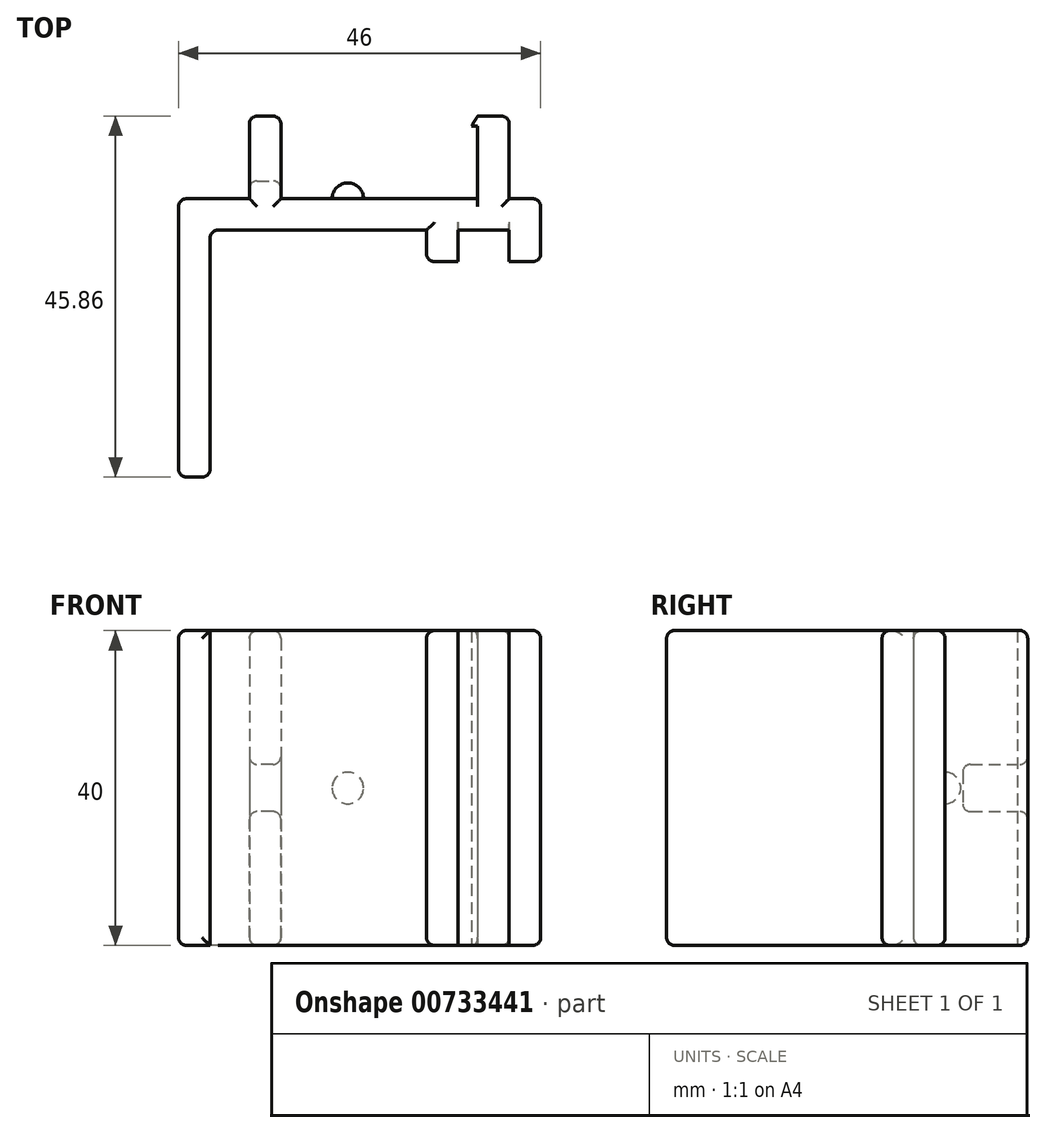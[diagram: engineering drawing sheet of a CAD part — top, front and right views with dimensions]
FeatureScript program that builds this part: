
annotation { "Feature Type Name" : "Feature", "Feature Type Description" : "" }
export const myFeature = defineFeature(function(context is Context, id is Id, definition is map)
    precondition{}
    {
        {
            var Q0;
            Q0=qCreatedBy(makeId("Top.planeOp"),FACE);
            var sketch = newSketch(context, id + "F0", { "sketchPlane" : qUnion([Q0])});
            skLineSegment(sketch, "E0", {"start": v(-21.66, 16.4) * mm, "end": v(-12.66, 16.4) * mm});
            skLineSegment(sketch, "E1", {"start": v(24.34, 16.4) * mm, "end": v(24.34, 8.4) * mm});
            skLineSegment(sketch, "E2", {"start": v(24.34, 8.4) * mm, "end": v(20.34, 8.4) * mm});
            skLineSegment(sketch, "E3", {"start": v(20.34, 8.4) * mm, "end": v(20.34, 12.4) * mm});
            skLineSegment(sketch, "E4", {"start": v(20.34, 12.4) * mm, "end": v(13.84, 12.4) * mm});
            skLineSegment(sketch, "E5", {"start": v(-17.66, 12.4) * mm, "end": v(-17.66, -18.96) * mm});
            skLineSegment(sketch, "E6", {"start": v(-17.66, -18.96) * mm, "end": v(-21.66, -18.96) * mm});
            skLineSegment(sketch, "E7", {"start": v(-21.66, -18.96) * mm, "end": v(-21.66, 16.4) * mm});
            skLineSegment(sketch, "E8", {"start": v(20.34, 16.4) * mm, "end": v(20.34, 26.9) * mm});
            skLineSegment(sketch, "E9", {"start": v(20.34, 26.9) * mm, "end": v(16.34, 26.9) * mm});
            skLineSegment(sketch, "E10", {"start": v(16.34, 25.6) * mm, "end": v(16.34, 16.4) * mm});
            skLineSegment(sketch, "E11", {"start": v(16.34, 26.9) * mm, "end": v(15.54, 25.6) * mm});
            skLineSegment(sketch, "E12", {"start": v(15.54, 25.6) * mm, "end": v(16.34, 25.6) * mm});
            skLineSegment(sketch, "E13", {"start": v(-12.66, 18.65) * mm, "end": v(-8.66, 18.65) * mm});
            skLineSegment(sketch, "E14.trimOffspring", {"start": v(-8.66, 16.4) * mm, "end": v(16.34, 16.4) * mm});
            skLineSegment(sketch, "E15.trimOffspring", {"start": v(20.34, 16.4) * mm, "end": v(24.34, 16.4) * mm});
            skLineSegment(sketch, "E16", {"start": v(13.84, 12.4) * mm, "end": v(13.84, 8.4) * mm});
            skLineSegment(sketch, "E17", {"start": v(13.84, 8.4) * mm, "end": v(9.84, 8.4) * mm});
            skLineSegment(sketch, "E18", {"start": v(9.84, 8.4) * mm, "end": v(9.84, 12.4) * mm});
            skLineSegment(sketch, "E19.trimOffspring", {"start": v(9.84, 12.4) * mm, "end": v(-17.66, 12.4) * mm});
            skLineSegment(sketch, "E20", {"start": v(-12.66, 18.65) * mm, "end": v(-12.66, 16.4) * mm});
            skLineSegment(sketch, "E21", {"start": v(-8.66, 18.65) * mm, "end": v(-8.66, 16.4) * mm});
            skSolve(sketch);
        }
        {
            var Q0;
            {var subQ0=sQuery(id+"F0.wireOp",EDGE,"E0");Q0=makeQuery(id+"F0.imprint","IMPRINT",FACE,{"disambiguationData":[TD([[makeQuery(id+"F0.imprint","IMPRINT",EDGE,{"derivedFrom":subQ0}),-1.0]])]});}
            extrude(context, id + "F1", {"entities" : qUnion([Q0]), "depth" : 40 * mm, "offsetDistance" : 25 * mm});
        }
        {
            var Q0;
            Q0=makeQuery(id+"F1.opExtrude","SWEPT_FACE",FACE,{"disambiguationData":[OSD([sQuery(id+"F0.wireOp",EDGE,"E20")])]});
            var sketch = newSketch(context, id + "F2", { "sketchPlane" : qUnion([Q0])});
            skLineSegment(sketch, "E22.bottom", {"start": v(-16.4, 0) * mm, "end": v(-26.9, 0) * mm});
            skLineSegment(sketch, "E22.top", {"start": v(-16.4, 17) * mm, "end": v(-26.9, 17) * mm});
            skLineSegment(sketch, "E22.left", {"start": v(-16.4, 0) * mm, "end": v(-16.4, 17) * mm});
            skLineSegment(sketch, "E22.right", {"start": v(-26.9, 0) * mm, "end": v(-26.9, 17) * mm});
            skLineSegment(sketch, "E23.bottom", {"start": v(-16.4, 40) * mm, "end": v(-26.9, 40) * mm});
            skLineSegment(sketch, "E23.top", {"start": v(-16.4, 23) * mm, "end": v(-26.9, 23) * mm});
            skLineSegment(sketch, "E23.left", {"start": v(-16.4, 40) * mm, "end": v(-16.4, 23) * mm});
            skLineSegment(sketch, "E23.right", {"start": v(-26.9, 40) * mm, "end": v(-26.9, 23) * mm});
            skSolve(sketch);
        }
        {
            var Q0;
            Q0 = qSketchRegion(id + "F2", true);
            var Q1;
            Q1=makeQuery(id+"F1.opExtrude","SWEPT_FACE",FACE,{"disambiguationData":[OSD([sQuery(id+"F0.wireOp",EDGE,"E21")])]});
            extrude(context, id + "F3", {"entities" : qUnion([Q0]), "operationType" : NewBodyOperationType.ADD, "endBound" : BoundingType.UP_TO_SURFACE, "oppositeDirection" : true, "depth" : 17 * mm, "endBoundEntityFace" : qUnion([Q1]), "offsetDistance" : 25 * mm});
        }
        {
            var Q0;
            Q0=makeQuery(id+"F1.opExtrude","SWEPT_EDGE",EDGE,{"disambiguationData":[OSD([sQuery(id+"F0.wireOp",EDGE,"E8"),sQuery(id+"F0.wireOp",EDGE,"E9")])]});
            var Q1;
            Q1=makeQuery(id+"F3.boolean.opBoolean","INTERSECT",EDGE,{"derivedFrom":[makeQuery(id+"F1.opExtrude","SWEPT_FACE",FACE,{"disambiguationData":[OSD([sQuery(id+"F0.wireOp",EDGE,"E13")])]}),makeQuery(id+"F3.opExtrude","SWEPT_FACE",FACE,{"disambiguationData":[OSD([sQuery(id+"F2.wireOp",EDGE,"E22.top")])]})]});
            var Q2;
            Q2=makeQuery(id+"F3.boolean.opBoolean","INTERSECT",EDGE,{"derivedFrom":[makeQuery(id+"F1.opExtrude","SWEPT_FACE",FACE,{"disambiguationData":[OSD([sQuery(id+"F0.wireOp",EDGE,"E13")])]}),makeQuery(id+"F3.opExtrude","SWEPT_FACE",FACE,{"disambiguationData":[OSD([sQuery(id+"F2.wireOp",EDGE,"E23.top")])]})]});
            var Q3;
            Q3=makeQuery(id+"F3.opExtrude","SWEPT_EDGE",EDGE,{"disambiguationData":[OSD([sQuery(id+"F2.wireOp",EDGE,"E22.top"),sQuery(id+"F2.wireOp",EDGE,"E22.right")])]});
            var Q4;
            Q4=makeQuery(id+"F3.opExtrude","SWEPT_EDGE",EDGE,{"disambiguationData":[OSD([sQuery(id+"F2.wireOp",EDGE,"E23.top"),sQuery(id+"F2.wireOp",EDGE,"E23.right")])]});
            var Q5;
            Q5=makeQuery(id+"F3.opExtrude","SWEPT_EDGE",EDGE,{"disambiguationData":[OSD([sQuery(id+"F2.wireOp",EDGE,"E22.bottom"),sQuery(id+"F2.wireOp",EDGE,"E22.right")])]});
            var Q6;
            Q6=makeQuery(id+"F3.opExtrude","SWEPT_EDGE",EDGE,{"disambiguationData":[OSD([sQuery(id+"F2.wireOp",EDGE,"E23.bottom"),sQuery(id+"F2.wireOp",EDGE,"E23.right")])]});
            var Q7;
            Q7=makeQuery(id+"F1.opExtrude","SWEPT_EDGE",EDGE,{"disambiguationData":[OSD([sQuery(id+"F0.wireOp",EDGE,"E1"),sQuery(id+"F0.wireOp",EDGE,"E2")])]});
            var Q8;
            Q8=makeQuery(id+"F1.opExtrude","SWEPT_EDGE",EDGE,{"disambiguationData":[OSD([sQuery(id+"F0.wireOp",EDGE,"E17"),sQuery(id+"F0.wireOp",EDGE,"E18")])]});
            var Q9;
            Q9=makeQuery(id+"F1.opExtrude","SWEPT_EDGE",EDGE,{"disambiguationData":[OSD([sQuery(id+"F0.wireOp",EDGE,"E5"),sQuery(id+"F0.wireOp",EDGE,"E19.trimOffspring")])]});
            var Q10;
            Q10=makeQuery(id+"F1.opExtrude","SWEPT_EDGE",EDGE,{"disambiguationData":[OSD([sQuery(id+"F0.wireOp",EDGE,"E6"),sQuery(id+"F0.wireOp",EDGE,"E7")])]});
            var Q11;
            Q11=makeQuery(id+"F3.boolean.opBoolean","MERGE",EDGE,{"derivedFrom":[makeQuery(id+"F1.opExtrude","CAP_EDGE",EDGE,{"disambiguationData":[OSD([sQuery(id+"F0.wireOp",EDGE,"E20")])],"isStart":false}),makeQuery(id+"F3.opExtrude","CAP_EDGE",EDGE,{"disambiguationData":[OSD([sQuery(id+"F2.wireOp",EDGE,"E23.bottom")])],"isStart":true})]});
            var Q12;
            Q12=makeQuery(id+"F3.boolean.opBoolean","MERGE",EDGE,{"derivedFrom":[makeQuery(id+"F1.opExtrude","CAP_EDGE",EDGE,{"disambiguationData":[OSD([sQuery(id+"F0.wireOp",EDGE,"E20")])],"isStart":true}),makeQuery(id+"F3.opExtrude","CAP_EDGE",EDGE,{"disambiguationData":[OSD([sQuery(id+"F2.wireOp",EDGE,"E22.bottom")])],"isStart":true})]});
            var Q13;
            Q13=makeQuery(id+"F3.opExtrude","CAP_EDGE",EDGE,{"disambiguationData":[OSD([sQuery(id+"F2.wireOp",EDGE,"E22.right")])],"isStart":true});
            var Q14;
            Q14=makeQuery(id+"F3.opExtrude","CAP_EDGE",EDGE,{"disambiguationData":[OSD([sQuery(id+"F2.wireOp",EDGE,"E23.right")])],"isStart":true});
            var Q15;
            Q15=makeQuery(id+"F1.opExtrude","CAP_EDGE",EDGE,{"disambiguationData":[OSD([sQuery(id+"F0.wireOp",EDGE,"E0")])],"isStart":true});
            var Q16;
            Q16=makeQuery(id+"F1.opExtrude","CAP_EDGE",EDGE,{"disambiguationData":[OSD([sQuery(id+"F0.wireOp",EDGE,"E0")])],"isStart":false});
            var Q17;
            Q17=makeQuery(id+"F1.opExtrude","CAP_EDGE",EDGE,{"disambiguationData":[OSD([sQuery(id+"F0.wireOp",EDGE,"E7")])],"isStart":false});
            var Q18;
            Q18=makeQuery(id+"F1.opExtrude","CAP_EDGE",EDGE,{"disambiguationData":[OSD([sQuery(id+"F0.wireOp",EDGE,"E7")])],"isStart":true});
            var Q19;
            Q19=makeQuery(id+"F1.opExtrude","CAP_EDGE",EDGE,{"disambiguationData":[OSD([sQuery(id+"F0.wireOp",EDGE,"E6")])],"isStart":false});
            var Q20;
            Q20=makeQuery(id+"F1.opExtrude","CAP_EDGE",EDGE,{"disambiguationData":[OSD([sQuery(id+"F0.wireOp",EDGE,"E6")])],"isStart":true});
            var Q21;
            Q21=makeQuery(id+"F1.opExtrude","CAP_EDGE",EDGE,{"disambiguationData":[OSD([sQuery(id+"F0.wireOp",EDGE,"E9")])],"isStart":true});
            var Q22;
            Q22=makeQuery(id+"F1.opExtrude","CAP_EDGE",EDGE,{"disambiguationData":[OSD([sQuery(id+"F0.wireOp",EDGE,"E9")])],"isStart":false});
            var Q23;
            Q23=makeQuery(id+"F1.opExtrude","CAP_EDGE",EDGE,{"disambiguationData":[OSD([sQuery(id+"F0.wireOp",EDGE,"E8")])],"isStart":true});
            var Q24;
            Q24=makeQuery(id+"F1.opExtrude","CAP_EDGE",EDGE,{"disambiguationData":[OSD([sQuery(id+"F0.wireOp",EDGE,"E8")])],"isStart":false});
            var Q25;
            Q25=makeQuery(id+"F1.opExtrude","CAP_EDGE",EDGE,{"disambiguationData":[OSD([sQuery(id+"F0.wireOp",EDGE,"E14.trimOffspring")])],"isStart":true});
            var Q26;
            Q26=makeQuery(id+"F1.opExtrude","CAP_EDGE",EDGE,{"disambiguationData":[OSD([sQuery(id+"F0.wireOp",EDGE,"E14.trimOffspring")])],"isStart":false});
            var Q27;
            Q27=makeQuery(id+"F1.opExtrude","CAP_EDGE",EDGE,{"disambiguationData":[OSD([sQuery(id+"F0.wireOp",EDGE,"E19.trimOffspring")])],"isStart":true});
            var Q28;
            Q28=makeQuery(id+"F1.opExtrude","CAP_EDGE",EDGE,{"disambiguationData":[OSD([sQuery(id+"F0.wireOp",EDGE,"E19.trimOffspring")])],"isStart":false});
            var Q29;
            Q29=makeQuery(id+"F1.opExtrude","SWEPT_EDGE",EDGE,{"disambiguationData":[OSD([sQuery(id+"F0.wireOp",EDGE,"E5"),sQuery(id+"F0.wireOp",EDGE,"E6")])]});
            var Q30;
            Q30=makeQuery(id+"F3.boolean.opBoolean","MERGE",EDGE,{"derivedFrom":[makeQuery(id+"F1.opExtrude","CAP_EDGE",EDGE,{"disambiguationData":[OSD([sQuery(id+"F0.wireOp",EDGE,"E21")])],"isStart":true}),makeQuery(id+"F3.opExtrude","CAP_EDGE",EDGE,{"disambiguationData":[OSD([sQuery(id+"F2.wireOp",EDGE,"E22.bottom")])],"isStart":false})]});
            var Q31;
            Q31=makeQuery(id+"F3.opExtrude","CAP_EDGE",EDGE,{"disambiguationData":[OSD([sQuery(id+"F2.wireOp",EDGE,"E22.right")])],"isStart":false});
            var Q32;
            Q32=makeQuery(id+"F3.opExtrude","CAP_EDGE",EDGE,{"disambiguationData":[OSD([sQuery(id+"F2.wireOp",EDGE,"E23.right")])],"isStart":false});
            var Q33;
            Q33=makeQuery(id+"F3.boolean.opBoolean","MERGE",EDGE,{"derivedFrom":[makeQuery(id+"F1.opExtrude","CAP_EDGE",EDGE,{"disambiguationData":[OSD([sQuery(id+"F0.wireOp",EDGE,"E21")])],"isStart":false}),makeQuery(id+"F3.opExtrude","CAP_EDGE",EDGE,{"disambiguationData":[OSD([sQuery(id+"F2.wireOp",EDGE,"E23.bottom")])],"isStart":false})]});
            var Q34;
            Q34=makeQuery(id+"F3.opExtrude","CAP_EDGE",EDGE,{"disambiguationData":[OSD([sQuery(id+"F2.wireOp",EDGE,"E22.top")])],"isStart":true});
            var Q35;
            Q35=makeQuery(id+"F3.opExtrude","CAP_EDGE",EDGE,{"disambiguationData":[OSD([sQuery(id+"F2.wireOp",EDGE,"E22.top")])],"isStart":false});
            var Q36;
            Q36=makeQuery(id+"F1.opExtrude","SWEPT_EDGE",EDGE,{"disambiguationData":[OSD([sQuery(id+"F0.wireOp",EDGE,"E13"),sQuery(id+"F0.wireOp",EDGE,"E21")])]});
            var Q37;
            Q37=makeQuery(id+"F1.opExtrude","SWEPT_EDGE",EDGE,{"disambiguationData":[OSD([sQuery(id+"F0.wireOp",EDGE,"E13"),sQuery(id+"F0.wireOp",EDGE,"E20")])]});
            var Q38;
            Q38=makeQuery(id+"F3.opExtrude","CAP_EDGE",EDGE,{"disambiguationData":[OSD([sQuery(id+"F2.wireOp",EDGE,"E23.top")])],"isStart":true});
            var Q39;
            Q39=makeQuery(id+"F3.opExtrude","CAP_EDGE",EDGE,{"disambiguationData":[OSD([sQuery(id+"F2.wireOp",EDGE,"E23.top")])],"isStart":false});
            var Q40;
            Q40=makeQuery(id+"F1.opExtrude","CAP_EDGE",EDGE,{"disambiguationData":[OSD([sQuery(id+"F0.wireOp",EDGE,"E15.trimOffspring")])],"isStart":true});
            var Q41;
            Q41=makeQuery(id+"F1.opExtrude","CAP_EDGE",EDGE,{"disambiguationData":[OSD([sQuery(id+"F0.wireOp",EDGE,"E1")])],"isStart":true});
            var Q42;
            Q42=makeQuery(id+"F1.opExtrude","CAP_EDGE",EDGE,{"disambiguationData":[OSD([sQuery(id+"F0.wireOp",EDGE,"E2")])],"isStart":true});
            var Q43;
            Q43=makeQuery(id+"F1.opExtrude","CAP_EDGE",EDGE,{"disambiguationData":[OSD([sQuery(id+"F0.wireOp",EDGE,"E18")])],"isStart":true});
            var Q44;
            Q44=makeQuery(id+"F1.opExtrude","CAP_EDGE",EDGE,{"disambiguationData":[OSD([sQuery(id+"F0.wireOp",EDGE,"E17")])],"isStart":true});
            var Q45;
            Q45=makeQuery(id+"F1.opExtrude","CAP_EDGE",EDGE,{"disambiguationData":[OSD([sQuery(id+"F0.wireOp",EDGE,"E4")])],"isStart":true});
            var Q46;
            Q46=makeQuery(id+"F1.opExtrude","CAP_EDGE",EDGE,{"disambiguationData":[OSD([sQuery(id+"F0.wireOp",EDGE,"E1")])],"isStart":false});
            var Q47;
            Q47=makeQuery(id+"F1.opExtrude","CAP_EDGE",EDGE,{"disambiguationData":[OSD([sQuery(id+"F0.wireOp",EDGE,"E2")])],"isStart":false});
            var Q48;
            Q48=makeQuery(id+"F1.opExtrude","CAP_EDGE",EDGE,{"disambiguationData":[OSD([sQuery(id+"F0.wireOp",EDGE,"E17")])],"isStart":false});
            var Q49;
            Q49=makeQuery(id+"F1.opExtrude","CAP_EDGE",EDGE,{"disambiguationData":[OSD([sQuery(id+"F0.wireOp",EDGE,"E18")])],"isStart":false});
            var Q50;
            Q50=makeQuery(id+"F1.opExtrude","CAP_EDGE",EDGE,{"disambiguationData":[OSD([sQuery(id+"F0.wireOp",EDGE,"E15.trimOffspring")])],"isStart":false});
            var Q51;
            Q51=makeQuery(id+"F1.opExtrude","SWEPT_EDGE",EDGE,{"disambiguationData":[OSD([sQuery(id+"F0.wireOp",EDGE,"E1"),sQuery(id+"F0.wireOp",EDGE,"E15.trimOffspring")])]});
            var Q52;
            Q52=makeQuery(id+"F1.opExtrude","SWEPT_EDGE",EDGE,{"disambiguationData":[OSD([sQuery(id+"F0.wireOp",EDGE,"E0"),sQuery(id+"F0.wireOp",EDGE,"E7")])]});
            fillet(context, id + "F4", {"entities" : qUnion([Q0, Q1, Q2, Q3, Q4, Q5, Q6, Q7, Q8, Q9, Q10, Q11, Q12, Q13, Q14, Q15, Q16, Q17, Q18, Q19, Q20, Q21, Q22, Q23, Q24, Q25, Q26, Q27, Q28, Q29, Q30, Q31, Q32, Q33, Q34, Q35, Q36, Q37, Q38, Q39, Q40, Q41, Q42, Q43, Q44, Q45, Q46, Q47, Q48, Q49, Q50, Q51, Q52]), "radius" : 1 * mm, "tangentPropagation" : true, "defaultsChanged" : false, "vertexSettings" : [], "allowEdgeOverflow" : false});
        }
        {
            var Q0;
            Q0=makeQuery(id+"F1.opExtrude","SWEPT_FACE",FACE,{"disambiguationData":[OSD([sQuery(id+"F0.wireOp",EDGE,"E14.trimOffspring")])]});
            var sketch = newSketch(context, id + "F5", { "sketchPlane" : qUnion([Q0])});
            skArc(sketch, "E24", {"start": v(-1.84, 20) * mm, "mid": v(0.16, 18) * mm, "end": v(2.16, 20) * mm});
            skLineSegment(sketch, "E25", {"start": v(-16.34, 20) * mm, "end": v(-16.34, 20) * mm});
            skLineSegment(sketch, "E26", {"start": v(-1.84, 20) * mm, "end": v(2.16, 20) * mm});
            skSolve(sketch);
        }
        {
            var Q0;
            Q0=makeQuery(id+"F5.imprint","IMPRINT",FACE,{"disambiguationData":[TD([[makeQuery(id+"F5.imprint","IMPRINT",EDGE,{"derivedFrom":sQuery(id+"F5.wireOp",EDGE,"E24")}),1.0]])]});
            var Q1;
            Q1=sQuery(id+"F5.wireOp",EDGE,"E26");
            revolve(context, id + "F6", {"operationType" : NewBodyOperationType.ADD, "surfaceOperationType" : NewSurfaceOperationType.NEW, "entities" : qUnion([Q0]), "axis" : qUnion([Q1]), "revolveType" : RevolveType.FULL});
        }
    });
